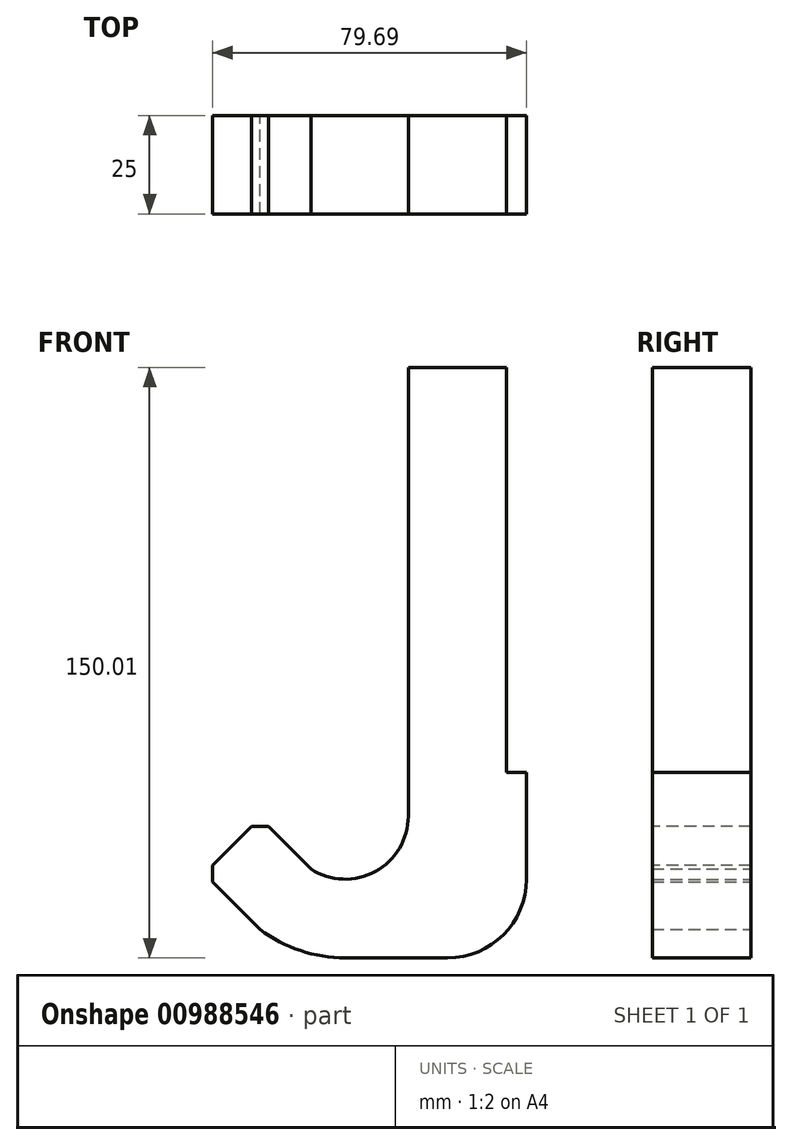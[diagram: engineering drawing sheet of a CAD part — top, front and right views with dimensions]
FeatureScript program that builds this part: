
annotation { "Feature Type Name" : "Feature", "Feature Type Description" : "" }
export const myFeature = defineFeature(function(context is Context, id is Id, definition is map)
    precondition{}
    {
        {
            var Q0;
            Q0=qCreatedBy(makeId("Front.planeOp"),FACE);
            var sketch = newSketch(context, id + "F0", { "sketchPlane" : qUnion([Q0])});
            skLineSegment(sketch, "E0", {"start": v(0, 114) * mm, "end": v(0, 0) * mm});
            skArc(sketch, "E1", {"start": v(0, 0) * mm, "mid": v(-8.37, -14.06) * mm, "end": v(-24.72, -13.42) * mm});
            skLineSegment(sketch, "E2", {"start": v(-37.67, -0.46) * mm, "end": v(-51.82, -14.6) * mm});
            skLineSegment(sketch, "E3", {"start": v(-51.82, -14.6) * mm, "end": v(-37.67, -28.74) * mm});
            skLineSegment(sketch, "E4", {"start": v(-16, -36) * mm, "end": v(10, -36) * mm});
            skLineSegment(sketch, "E5", {"start": v(30, -16) * mm, "end": v(30, 11.19) * mm});
            skLineSegment(sketch, "E6", {"start": v(30, 11.19) * mm, "end": v(25, 11.19) * mm});
            skLineSegment(sketch, "E7", {"start": v(25, 11.19) * mm, "end": v(25, 114) * mm});
            skLineSegment(sketch, "E8", {"start": v(25, 114) * mm, "end": v(0, 114) * mm});
            skPoint(sketch, "E9.visualSharp", {"position": v(30, -36) * mm});
            skArc(sketch, "E9.filletArc", {"start": v(10, -36) * mm, "mid": v(24.14, -30.14) * mm, "end": v(30, -16) * mm});
            skArc(sketch, "E10", {"start": v(-37.67, -28.74) * mm, "mid": v(-27.43, -34.14) * mm, "end": v(-16, -36) * mm});
            skPoint(sketch, "E11.start.orphan", {"position": v(-37.67, -28.74) * mm});
            skLineSegment(sketch, "E12", {"start": v(-24.72, -13.42) * mm, "end": v(-37.67, -0.46) * mm});
            skSolve(sketch);
        }
        {
            var Q0;
            Q0=makeQuery(id+"F0.imprint","IMPRINT",FACE,{"disambiguationData":[TD([[makeQuery(id+"F0.imprint","IMPRINT",EDGE,{"derivedFrom":sQuery(id+"F0.wireOp",EDGE,"E0")}),1.0]])]});
            extrude(context, id + "F1", {"entities" : qUnion([Q0]), "depth" : 25 * mm, "offsetDistance" : 25 * mm});
        }
        {
            var Q0;
            Q0=makeQuery(id+"F1.opExtrude","SWEPT_EDGE",EDGE,{"disambiguationData":[OSD([sQuery(id+"F0.wireOp",EDGE,"E2"),sQuery(id+"F0.wireOp",EDGE,"E12")])]});
            var Q1;
            Q1=makeQuery(id+"F1.opExtrude","SWEPT_EDGE",EDGE,{"disambiguationData":[OSD([sQuery(id+"F0.wireOp",EDGE,"E2"),sQuery(id+"F0.wireOp",EDGE,"E3")])]});
            chamfer(context, id + "F2", {"entities" : qUnion([Q0, Q1]), "width" : 3 * mm, "tangentPropagation" : true});
        }
    });
